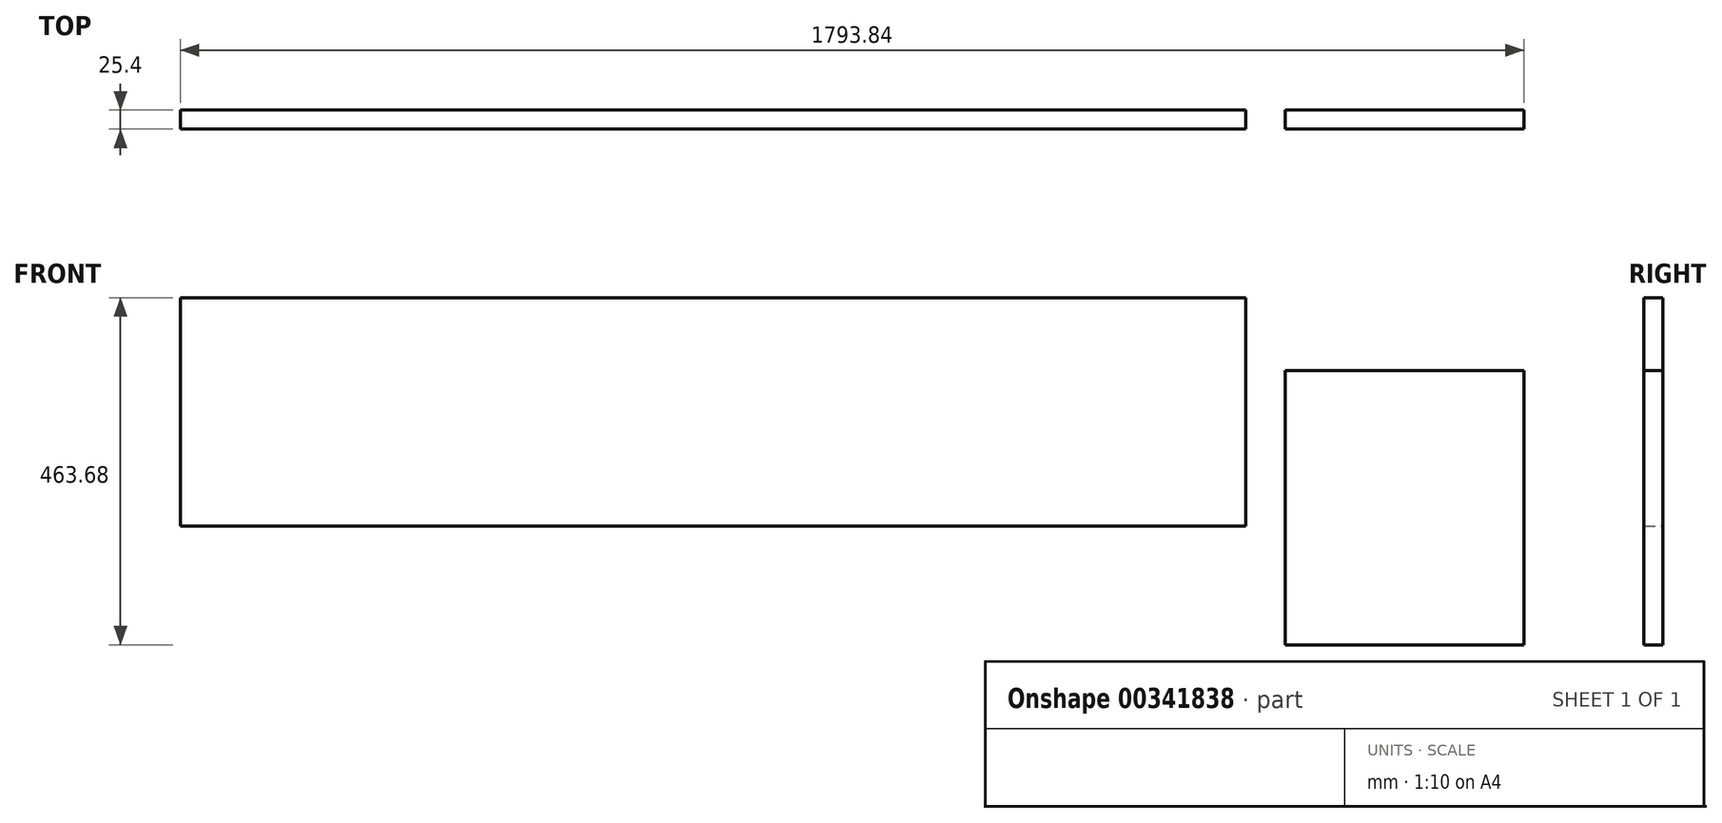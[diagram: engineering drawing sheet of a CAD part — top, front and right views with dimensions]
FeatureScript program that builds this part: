
annotation { "Feature Type Name" : "Feature", "Feature Type Description" : "" }
export const myFeature = defineFeature(function(context is Context, id is Id, definition is map)
    precondition{}
    {
        {
            var Q0;
            Q0=qCreatedBy(makeId("Front.planeOp"),FACE);
            var sketch = newSketch(context, id + "F0", { "sketchPlane" : qUnion([Q0])});
            skLineSegment(sketch, "E0.bottom", {"start": v(-104.47, 153.07) * mm, "end": v(214.01, 153.07) * mm});
            skLineSegment(sketch, "E0.top", {"start": v(-104.47, -213.29) * mm, "end": v(214.01, -213.29) * mm});
            skLineSegment(sketch, "E0.left", {"start": v(-104.47, 153.07) * mm, "end": v(-104.47, -213.29) * mm});
            skLineSegment(sketch, "E0.right", {"start": v(214.01, 153.07) * mm, "end": v(214.01, -213.29) * mm});
            skLineSegment(sketch, "E1.bottom", {"start": v(-1579.83, 250.39) * mm, "end": v(-157.43, 250.39) * mm});
            skLineSegment(sketch, "E1.top", {"start": v(-1579.83, -54.41) * mm, "end": v(-157.43, -54.41) * mm});
            skLineSegment(sketch, "E1.left", {"start": v(-1579.83, 250.39) * mm, "end": v(-1579.83, -54.41) * mm});
            skLineSegment(sketch, "E1.right", {"start": v(-157.43, 250.39) * mm, "end": v(-157.43, -54.41) * mm});
            skSolve(sketch);
        }
        {
            var Q0;
            Q0 = qSketchRegion(id + "F0", true);
            extrude(context, id + "F1", {"entities" : qUnion([Q0]), "depth" : 25.4 * mm});
        }
    });
